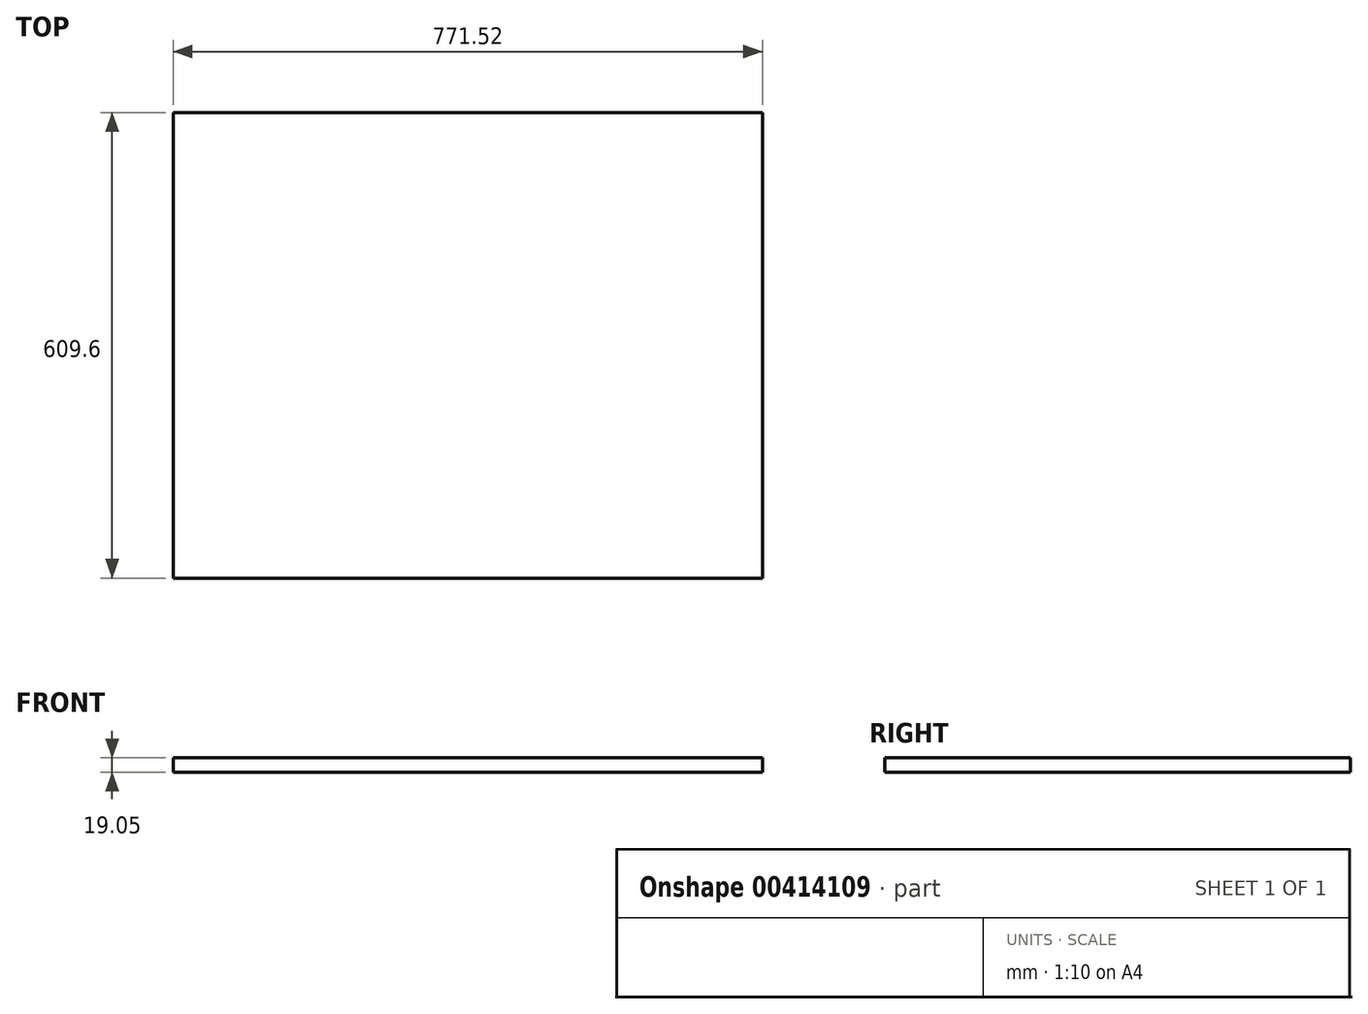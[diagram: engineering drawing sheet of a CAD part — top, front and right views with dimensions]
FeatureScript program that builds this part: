
annotation { "Feature Type Name" : "Feature", "Feature Type Description" : "" }
export const myFeature = defineFeature(function(context is Context, id is Id, definition is map)
    precondition{}
    {
        {
            var Q0;
            Q0=qCreatedBy(makeId("Top.planeOp"),FACE);
            var sketch = newSketch(context, id + "F0", { "sketchPlane" : qUnion([Q0])});
            skLineSegment(sketch, "E0.bottom", {"start": v(385.76, -304.8) * mm, "end": v(-385.76, -304.8) * mm});
            skLineSegment(sketch, "E0.top", {"start": v(385.76, 304.8) * mm, "end": v(-385.76, 304.8) * mm});
            skLineSegment(sketch, "E0.left", {"start": v(385.76, -304.8) * mm, "end": v(385.76, 304.8) * mm});
            skLineSegment(sketch, "E0.right", {"start": v(-385.76, -304.8) * mm, "end": v(-385.76, 304.8) * mm});
            skPoint(sketch, "E0.middle", {"position": v(0, 0) * mm});
            skSolve(sketch);
        }
        {
            var Q0;
            Q0=makeQuery(id+"F0.imprint","IMPRINT",FACE,{"disambiguationData":[TD([[makeQuery(id+"F0.imprint","IMPRINT",EDGE,{"derivedFrom":sQuery(id+"F0.wireOp",EDGE,"E0.bottom")}),-1.0]])]});
            extrude(context, id + "F1", {"entities" : qUnion([Q0]), "depth" : 19.05 * mm});
        }
    });
